# Revit family: 1000_Sliding_Window_XOX_Custom
name_source: partatom
category: Windows
revit_build: Autodesk Revit 2014 (Build: 20130308_1515(x64)
units: mm (PartAtom-declared; Revit-internal decimal feet)

## types (1)
- 1000SW-XOX-Custom
    Area Middle Sash Glazing = 0.75 m²
    Area Side Sash Glazing = 0.75 m²
    Centered In Wall = Yes
    Custom Frame Offset From Exterior = 0 mm  [stored 0 ft]
    Custom Sash Width Middle = 100 mm  [stored 0.328084 ft]
    Custom Windload = 1000 mm  [stored 3.28084 ft]
    Custom Window Height = 1200 mm  [stored 3.93701 ft]
    Custom Window Width = 2400 mm  [stored 7.87402 ft]
    Default Sill Height = 800 mm
    Description = sliding window, XOX custom
    Equal Sash Width = Yes
    Frame Thickness = 76 mm
    Heavy Duty Interlocker = No
    Height = 1200 mm  [stored 3.93701 ft]
    Is Heavy Duty Mullion = 0 mm  [stored 0 ft]
    Limit Sash Height Max = 1800 mm  [stored 5.90551 ft]
    Limit Sash Height Min = 300 mm
    Limit Sash Width Max = 1500 mm  [stored 4.92126 ft]
    Limit Sash Width Middle Max = 1500 mm  [stored 4.92126 ft]
    Limit Sash Width Middle Min = 300 mm
    Limit Sash Width Min = 300 mm
    Limit Window Height Max = 1857 mm
    Limit Window Height Min = 357 mm
    Limit Window Width Max = 4440 mm
    Limit Window Width Min = 840 mm  [stored 2.75591 ft]
    Manufacturer = Crealco
    Max Pane Area = 0.75 m²
    Model = 1000
    Sash Frame Seal = 2 mm  [stored 0.00656168 ft]
    Sash Height = 1143 mm  [stored 3.75 ft]
    Sash Width Middle = 820 mm
    Sash Width Sides = 820 mm
    Standard Interlocker = Yes
    URL = http://www.crealco.co.za
    Wall Closure = By host
    Width = 2400 mm  [stored 7.87402 ft]
    Windload Design = 1000 mm  [stored 3.28084 ft]

note: [stored X ft] marks values corroborated as IEEE doubles in the binary element streams (Revit-internal decimal feet)

## geometry (parser evidence)
native form markers: Sweep x12
no freeform markers — native parametric forms only
